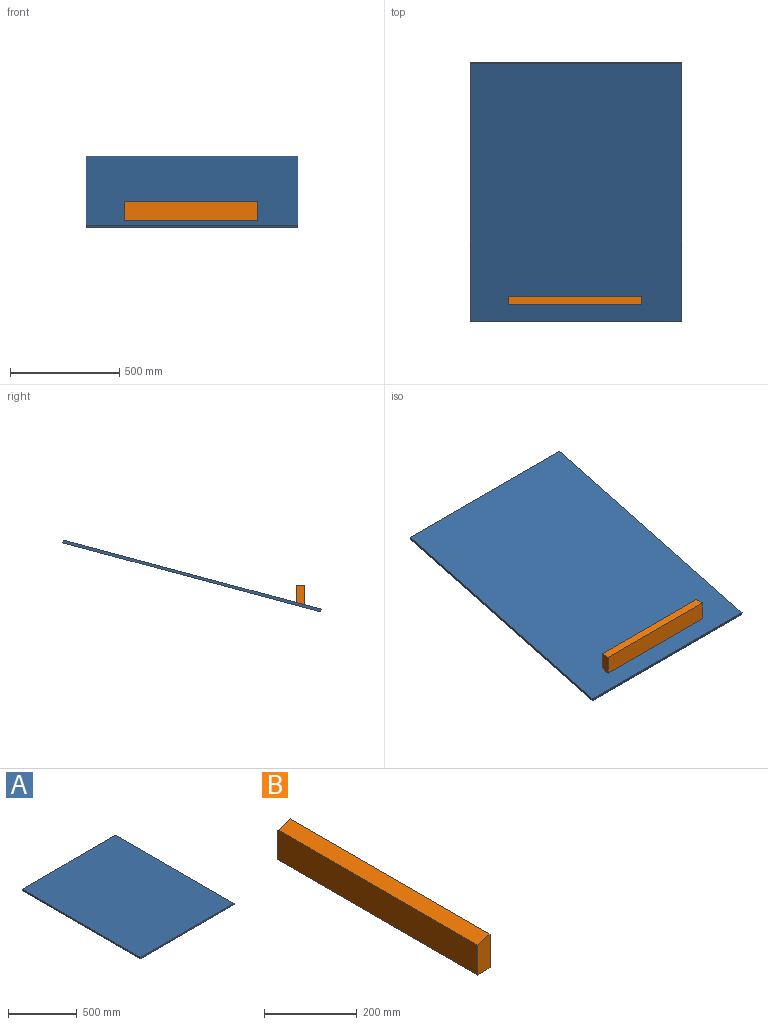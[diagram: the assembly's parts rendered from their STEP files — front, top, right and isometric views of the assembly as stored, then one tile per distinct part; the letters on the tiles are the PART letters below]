
ASSEMBLY  parts=2 mates=1
PART A: 6 faces, bbox 965.2x1219.2x12.7 mm
  f0: plane 965.2x12.7mm, normal (0,-1,0), area 12258mm2, adj f1,f3,f4,f5
  f1: plane 1219.2x12.7mm, normal (1,0,0), area 15483.8mm2, adj f0,f2,f4,f5
  f2: plane 965.2x12.7mm, normal (0,1,0), area 12258mm2, adj f1,f3,f4,f5
  f3: plane 1219.2x12.7mm, normal (-1,0,0), area 15483.8mm2, adj f0,f2,f4,f5
  f4: plane 1219.2x965.2mm, normal (0,0,1), area 1176771.8mm2, adj f0,f1,f2,f3
  f5: plane 1219.2x965.2mm, normal (0,0,-1), area 1176771.8mm2, adj f0,f1,f2,f3
PART B: 6 faces, bbox 38.1x609.6x89.2 mm
  f0: plane 609.6x38.1mm, normal (0.01,0,-1), area 23225.8mm2, adj f1,f3,f4,f5
  f1: plane 609.6x88.9mm, normal (1,0,0), area 54193.4mm2, adj f0,f2,f4,f5
  f2: plane 609.6x38.1mm, normal (-0.26,0,0.97), area 24044.8mm2, adj f1,f3,f4,f5
  f3: plane 609.6x78.96mm, normal (-1,0,0), area 48136.6mm2, adj f0,f2,f4,f5
  f4: plane 89.18x38.1mm, normal (0,-1,0), area 3197.7mm2, adj f0,f1,f2,f3
  f5: plane 89.18x38.1mm, normal (0,1,0), area 3197.7mm2, adj f0,f1,f2,f3
PLACE A rot(axis=(1,0,0),15deg) t=(10.78,420.78,-162.87)mm fixed
PLACE B rot(axis=(-0.71,0.71,0),180deg) t=(-297.84,-77.56,-243.94)mm
MATE planar A.f4 <-> B.f2  axis (0,-0.26,0.97) through (10.78,417.49,-150.61)mm
